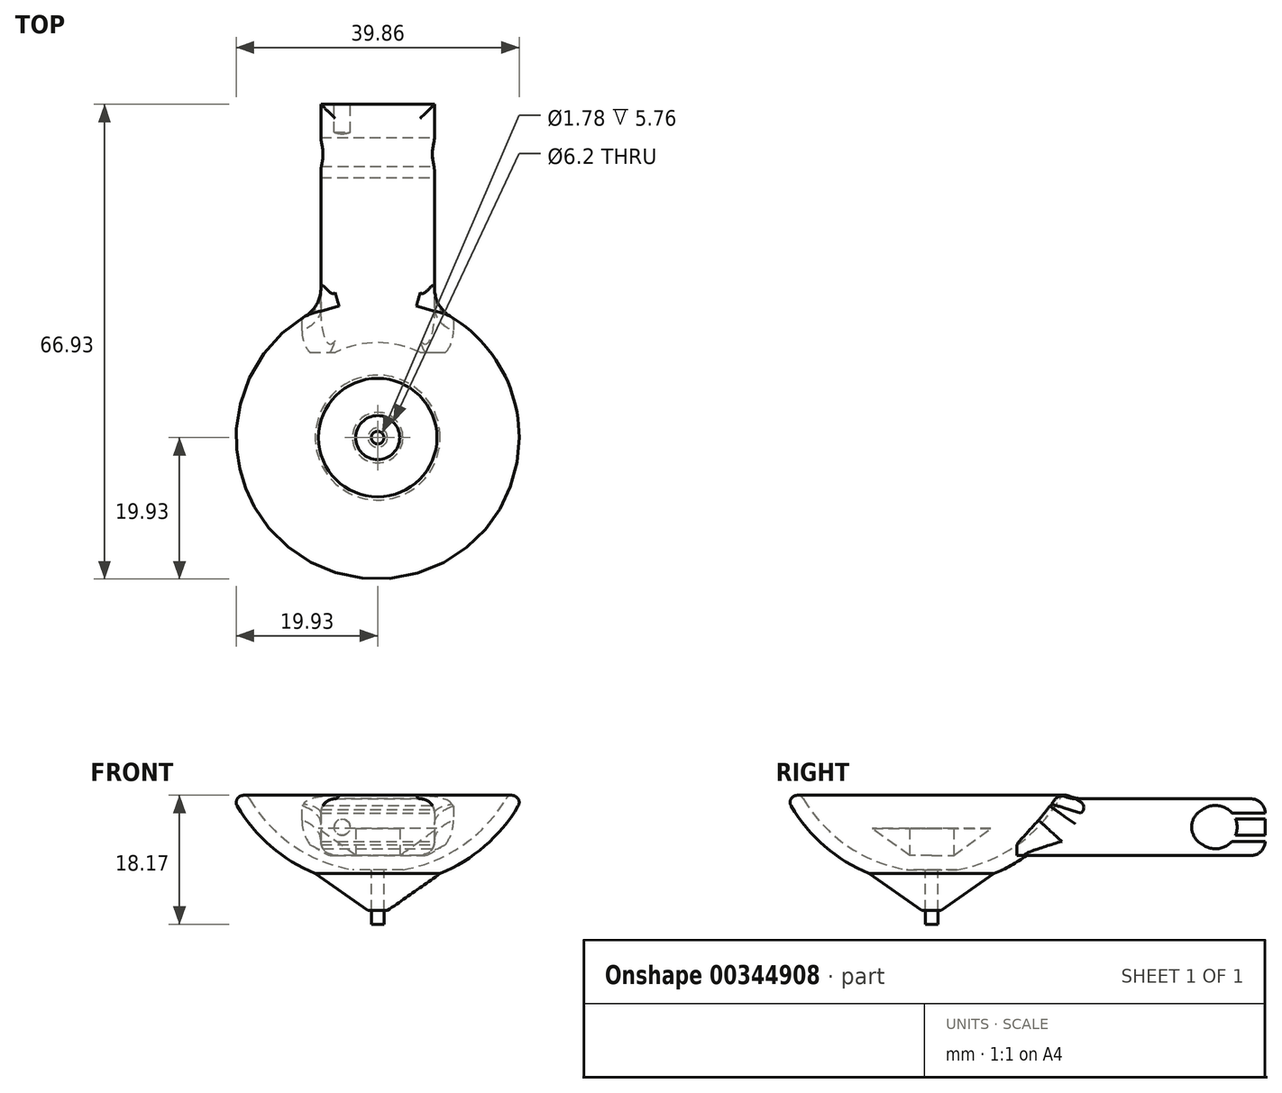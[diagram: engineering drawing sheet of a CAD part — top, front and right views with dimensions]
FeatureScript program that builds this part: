
annotation { "Feature Type Name" : "Feature", "Feature Type Description" : "" }
export const myFeature = defineFeature(function(context is Context, id is Id, definition is map)
    precondition{}
    {
        {
            var Q0;
            Q0=qCreatedBy(makeId("Right.planeOp"),FACE);
            var sketch = newSketch(context, id + "F0", { "sketchPlane" : qUnion([Q0])});
            skLineSegment(sketch, "E0", {"start": v(0, 0) * mm, "end": v(3.1, 0) * mm});
            skLineSegment(sketch, "E1.bottom", {"start": v(0, 0) * mm, "end": v(4.85, 0) * mm, "construction": true});
            skLineSegment(sketch, "E1.top", {"start": v(0, 1.3) * mm, "end": v(4.85, 1.3) * mm, "construction": true});
            skLineSegment(sketch, "E1.left", {"start": v(0, 0) * mm, "end": v(0, 1.3) * mm, "construction": true});
            skLineSegment(sketch, "E1.right", {"start": v(4.85, 0) * mm, "end": v(4.85, 1.3) * mm, "construction": true});
            skLineSegment(sketch, "E2.bottom", {"start": v(0, 0) * mm, "end": v(8.35, 0) * mm, "construction": true});
            skLineSegment(sketch, "E2.top", {"start": v(0, 3.8) * mm, "end": v(8.35, 3.8) * mm, "construction": true});
            skLineSegment(sketch, "E2.left", {"start": v(0, 0) * mm, "end": v(0, 3.8) * mm, "construction": true});
            skLineSegment(sketch, "E2.right", {"start": v(8.35, 0) * mm, "end": v(8.35, 3.8) * mm, "construction": true});
            skLineSegment(sketch, "E3", {"start": v(0, 0) * mm, "end": v(0, -2) * mm, "construction": true});
            skLineSegment(sketch, "E4", {"start": v(0, -2) * mm, "end": v(21.3, 12.36) * mm, "construction": true});
            skLineSegment(sketch, "E5", {"start": v(3.1, 0) * mm, "end": v(0, 0) * mm});
            skLineSegment(sketch, "E6", {"start": v(8.35, 3.8) * mm, "end": v(0, 3.8) * mm});
            skLineSegment(sketch, "E7", {"start": v(0, 3.8) * mm, "end": v(0, 0) * mm});
            skLineSegment(sketch, "E8", {"start": v(3.1, 0) * mm, "end": v(8.35, 3.8) * mm});
            skSolve(sketch);
        }
        {
            var Q0;
            Q0=makeQuery(id+"F0.imprint","IMPRINT",FACE,{"disambiguationData":[TD([[makeQuery(id+"F0.imprint","IMPRINT",EDGE,{"derivedFrom":sQuery(id+"F0.wireOp",EDGE,"E6")}),1.0]])]});
            var Q1;
            Q1=sQuery(id+"F0.wireOp",EDGE,"E7");
            revolve(context, id + "F1", {"entities" : qUnion([Q0]), "axis" : qUnion([Q1]), "revolveType" : RevolveType.FULL});
        }
        {
            var Q0;
            Q0=makeQuery(id+"F1.opRevolve","SWEPT_FACE",FACE,{"disambiguationData":[OSD([sQuery(id+"F0.wireOp",EDGE,"E0")])]});
            var sketch = newSketch(context, id + "F2", { "sketchPlane" : qUnion([Q0])});
            skCircle(sketch, "E9.0.0", {"center": v(0, 0) * mm, "radius": 3.1 * mm});
            skSolve(sketch);
        }
        {
            var Q0;
            Q0=makeQuery(id+"F2.imprint","IMPRINT",FACE,{"disambiguationData":[TD([[makeQuery(id+"F2.imprint","IMPRINT",EDGE,{"derivedFrom":sQuery(id+"F2.wireOp",EDGE,"E9.0.0")}),-1.0]])]});
            extrude(context, id + "F3", {"entities" : qUnion([Q0]), "oppositeDirection" : true, "depth" : 10 * mm});
        }
        {
            var Q0;
            Q0=makeQuery(id+"F2.imprint","IMPRINT",FACE,{"disambiguationData":[TD([[makeQuery(id+"F2.imprint","IMPRINT",EDGE,{"derivedFrom":sQuery(id+"F2.wireOp",EDGE,"E9.0.0")}),-1.0]])]});
            extrude(context, id + "F4", {"entities" : qUnion([Q0]), "operationType" : NewBodyOperationType.REMOVE, "oppositeDirection" : true, "depth" : 25 * mm});
        }
        {
            var Q0;
            Q0=qCreatedBy(makeId("Right.planeOp"),FACE);
            var sketch = newSketch(context, id + "F5", { "sketchPlane" : qUnion([Q0])});
            skLineSegment(sketch, "E10.bottom", {"start": v(0, -2) * mm, "end": v(0.89, -2) * mm});
            skLineSegment(sketch, "E10.top", {"start": v(0, -9.68) * mm, "end": v(0.89, -9.68) * mm});
            skLineSegment(sketch, "E10.left", {"start": v(0, -2) * mm, "end": v(0, -9.68) * mm});
            skLineSegment(sketch, "E10.right", {"start": v(0.89, -2) * mm, "end": v(0.89, -9.68) * mm});
            skSolve(sketch);
        }
        {
            var Q0;
            Q0=makeQuery(id+"F5.imprint","IMPRINT",FACE,{"disambiguationData":[TD([[makeQuery(id+"F5.imprint","IMPRINT",EDGE,{"derivedFrom":sQuery(id+"F5.wireOp",EDGE,"E10.bottom")}),-1.0]])]});
            var Q1;
            Q1=sQuery(id+"F5.wireOp",EDGE,"E10.left");
            revolve(context, id + "F6", {"entities" : qUnion([Q0]), "axis" : qUnion([Q1]), "revolveType" : RevolveType.FULL});
        }
        {
            var Q0;
            Q0=qCreatedBy(makeId("Right.planeOp"),FACE);
            var sketch = newSketch(context, id + "F7", { "sketchPlane" : qUnion([Q0])});
            skLineSegment(sketch, "E11", {"start": v(0.9, -2) * mm, "end": v(3.56, -2) * mm});
            skArc(sketch, "E12", {"start": v(3.56, -2) * mm, "mid": v(11.92, 1.4) * mm, "end": v(18.07, 8) * mm});
            skLineSegment(sketch, "E13", {"start": v(0, 8) * mm, "end": v(23.67, 8) * mm, "construction": true});
            skLineSegment(sketch, "E14.0", {"start": v(3.1, 0) * mm, "end": v(-3.1, 0) * mm});
            skLineSegment(sketch, "E15", {"start": v(0, 0) * mm, "end": v(8.87, 0) * mm, "construction": true});
            skLineSegment(sketch, "E16", {"start": v(0.89, -2) * mm, "end": v(0.9, -7.76) * mm});
            skLineSegment(sketch, "E17", {"start": v(0.9, -7.76) * mm, "end": v(1.37, -7.76) * mm});
            skArc(sketch, "E18.0", {"start": v(8.8, -2.55) * mm, "mid": v(15.07, 1.32) * mm, "end": v(19.8, 6.98) * mm});
            skLineSegment(sketch, "E19", {"start": v(8.8, -2.55) * mm, "end": v(1.37, -7.76) * mm});
            skArc(sketch, "E20", {"start": v(18.07, 8) * mm, "mid": v(19.44, 8.35) * mm, "end": v(19.8, 6.98) * mm});
            skLineSegment(sketch, "E21", {"start": v(0, 18.7) * mm, "end": v(0, -11.68) * mm, "construction": true});
            skSolve(sketch);
        }
        {
            var Q0;
            {var subQ4=sQuery(id+"F7.wireOp",EDGE,"E12");Q0=makeQuery(id+"F7.imprint","IMPRINT",FACE,{"disambiguationData":[TD([[makeQuery(id+"F7.imprint","IMPRINT",EDGE,{"derivedFrom":subQ4}),-1.0]])]});}
            var Q1;
            Q1=sQuery(id+"F7.wireOp",EDGE,"E21");
            revolve(context, id + "F8", {"entities" : qUnion([Q0]), "axis" : qUnion([Q1]), "revolveType" : RevolveType.FULL});
        }
        {
            var Q0;
            Q0=qCreatedBy(makeId("Right.planeOp"),FACE);
            var sketch = newSketch(context, id + "F9", { "sketchPlane" : qUnion([Q0])});
            skLineSegment(sketch, "E22.bottom", {"start": v(47, 8) * mm, "end": v(18.07, 8) * mm});
            skLineSegment(sketch, "E22.top", {"start": v(47, 0) * mm, "end": v(12, 0) * mm});
            skLineSegment(sketch, "E22.left", {"start": v(47, 8) * mm, "end": v(47, 0) * mm});
            skLineSegment(sketch, "E22.right", {"start": v(12, 1.46) * mm, "end": v(12, 0) * mm});
            skArc(sketch, "E23", {"start": v(12, 1.46) * mm, "mid": v(15.39, 4.4) * mm, "end": v(18.07, 8) * mm});
            skArc(sketch, "E24", {"start": v(38.23, 1.52) * mm, "mid": v(43.05, 4) * mm, "end": v(38.23, 6.48) * mm});
            skArc(sketch, "E25", {"start": v(38.23, 6.48) * mm, "mid": v(36.66, 4) * mm, "end": v(38.23, 1.52) * mm});
            skLineSegment(sketch, "E26", {"start": v(47, 4) * mm, "end": v(40, 4) * mm, "construction": true});
            skLineSegment(sketch, "E27", {"start": v(0, 0) * mm, "end": v(72.76, 0) * mm, "construction": true});
            skSolve(sketch);
        }
        {
            var Q0;
            Q0=makeQuery(id+"F9.imprint","IMPRINT",FACE,{"disambiguationData":[TD([[makeQuery(id+"F9.imprint","IMPRINT",EDGE,{"derivedFrom":sQuery(id+"F9.wireOp",EDGE,"E22.bottom")}),1.0]])]});
            extrude(context, id + "F10", {"entities" : qUnion([Q0]), "operationType" : NewBodyOperationType.ADD, "oppositeDirection" : true, "depth" : 8 * mm, "hasSecondDirection" : true, "secondDirectionOppositeDirection" : false, "secondDirectionDepth" : 8 * mm});
        }
        {
            var Q0;
            Q0=makeQuery(id+"F10.opExtrude","CAP_EDGE",EDGE,{"disambiguationData":[OSD([sQuery(id+"F9.wireOp",EDGE,"E22.bottom")])],"isStart":true});
            var Q1;
            Q1=makeQuery(id+"F10.opExtrude","CAP_EDGE",EDGE,{"disambiguationData":[OSD([sQuery(id+"F9.wireOp",EDGE,"E22.bottom")])],"isStart":false});
            var Q2;
            Q2=makeQuery(id+"F10.opExtrude","CAP_EDGE",EDGE,{"disambiguationData":[OSD([sQuery(id+"F9.wireOp",EDGE,"E22.top")])],"isStart":true});
            var Q3;
            Q3=makeQuery(id+"F10.opExtrude","CAP_EDGE",EDGE,{"disambiguationData":[OSD([sQuery(id+"F9.wireOp",EDGE,"E22.top")])],"isStart":false});
            var Q4;
            Q4=makeQuery(id+"F10.opExtrude","SWEPT_EDGE",EDGE,{"disambiguationData":[OSD([sQuery(id+"F9.wireOp",EDGE,"E22.bottom"),sQuery(id+"F9.wireOp",EDGE,"E22.left")])]});
            var Q5;
            Q5=makeQuery(id+"F10.opExtrude","SWEPT_EDGE",EDGE,{"disambiguationData":[OSD([sQuery(id+"F9.wireOp",EDGE,"E22.top"),sQuery(id+"F9.wireOp",EDGE,"E22.left")])]});
            fillet(context, id + "F11", {"entities" : qUnion([Q0, Q1, Q2, Q3, Q4, Q5]), "radius" : 2 * mm, "tangentPropagation" : true, "allowEdgeOverflow" : false});
        }
        {
            var Q0;
            Q0=makeQuery(id+"F10.boolean.opBoolean","INTERSECT",EDGE,{"derivedFrom":[makeQuery(id+"F8.opRevolve","SWEPT_FACE",FACE,{"disambiguationData":[OSD([sQuery(id+"F7.wireOp",EDGE,"E18.0")])]}),makeQuery(id+"F10.opExtrude","CAP_FACE",FACE,{"disambiguationData":[OSD([sQuery(id+"F9.wireOp",EDGE,"E22.bottom"),sQuery(id+"F9.wireOp",EDGE,"E22.top"),sQuery(id+"F9.wireOp",EDGE,"E22.left"),sQuery(id+"F9.wireOp",EDGE,"E22.right"),sQuery(id+"F9.wireOp",EDGE,"E23"),sQuery(id+"F9.wireOp",EDGE,"E24"),sQuery(id+"F9.wireOp",EDGE,"E25")])],"isStart":true})]});
            fillet(context, id + "F12", {"entities" : qUnion([Q0]), "radius" : 5 * mm, "tangentPropagation" : true, "allowEdgeOverflow" : false});
        }
        {
            var Q0;
            Q0=makeQuery(id+"F10.opExtrude","SWEPT_FACE",FACE,{"disambiguationData":[OSD([sQuery(id+"F9.wireOp",EDGE,"E22.left")])]});
            var sketch = newSketch(context, id + "F13", { "sketchPlane" : qUnion([Q0])});
            skLineSegment(sketch, "E28", {"start": v(0, 4) * mm, "end": v(-5, 4) * mm, "construction": true});
            skPoint(sketch, "E28.startSnap0", {"position": v(0, 2) * mm});
            skLineSegment(sketch, "E29", {"start": v(0, 6) * mm, "end": v(0, 2) * mm, "construction": true});
            skCircle(sketch, "E30", {"center": v(-5, 4) * mm, "radius": 1.13 * mm});
            skCircle(sketch, "E31.MirrorC", {"center": v(5, 4) * mm, "radius": 1.13 * mm});
            skSolve(sketch);
        }
        {
            var Q0;
            Q0=makeQuery(id+"F13.imprint","IMPRINT",FACE,{"disambiguationData":[TD([[makeQuery(id+"F13.imprint","IMPRINT",EDGE,{"derivedFrom":sQuery(id+"F13.wireOp",EDGE,"E30")}),1.0]])]});
            var Q1;
            Q1=makeQuery(id+"F13.imprint","IMPRINT",FACE,{"disambiguationData":[TD([[makeQuery(id+"F13.imprint","IMPRINT",EDGE,{"derivedFrom":sQuery(id+"F13.wireOp",EDGE,"E31.MirrorC")}),-1.0]])]});
            extrude(context, id + "F14", {"entities" : qUnion([Q0, Q1]), "operationType" : NewBodyOperationType.REMOVE, "oppositeDirection" : true, "depth" : 5 * mm});
        }
    });
